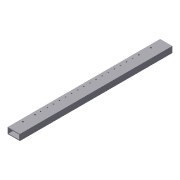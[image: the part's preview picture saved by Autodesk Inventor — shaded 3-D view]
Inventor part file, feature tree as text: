
AUTODESK INVENTOR PART (.ipt)
format: ipt  version: 2012 (Build 160160000, 160)  size: 127,488 bytes
history: native  units: in
note: dims shown in document units (in); Inventor stores cm internally (conversion verified against a paired STEP export)
features: extrude x3, sketch x3, shell x1
ambient origin geometry x8: Origin, YZ Plane, XZ Plane, XY Plane, X Axis, Y Axis, Z Axis, Center Point
bodies: Solid1 (feature_tree)
feature tree (7):
  extrude  "Extrusion1"  Depth=2.0in
  shell  "Shell1"  Thickness=25.0in
  extrude  "Extrusion2"  Depth=2.0in
  extrude  "Extrusion3"  Depth=0.25in
  sketch  "Sketch1"  dims[d0=1.0in d1=2.0in d2=25.0in d3=0.0in]
  sketch  "Sketch2"  dims[d4=0.5in d5=2.0in]
  sketch  "Sketch3"  dims[d6=2.0in d7=0.25in d8=0.25in d9=0.25in d10=0.25in d11=25.0in d12=0.0in d13=0.125in d14=0.5in d15=1.0in d16=5.0in d17=0.1875in d18=25.0in d19=0.0in]
